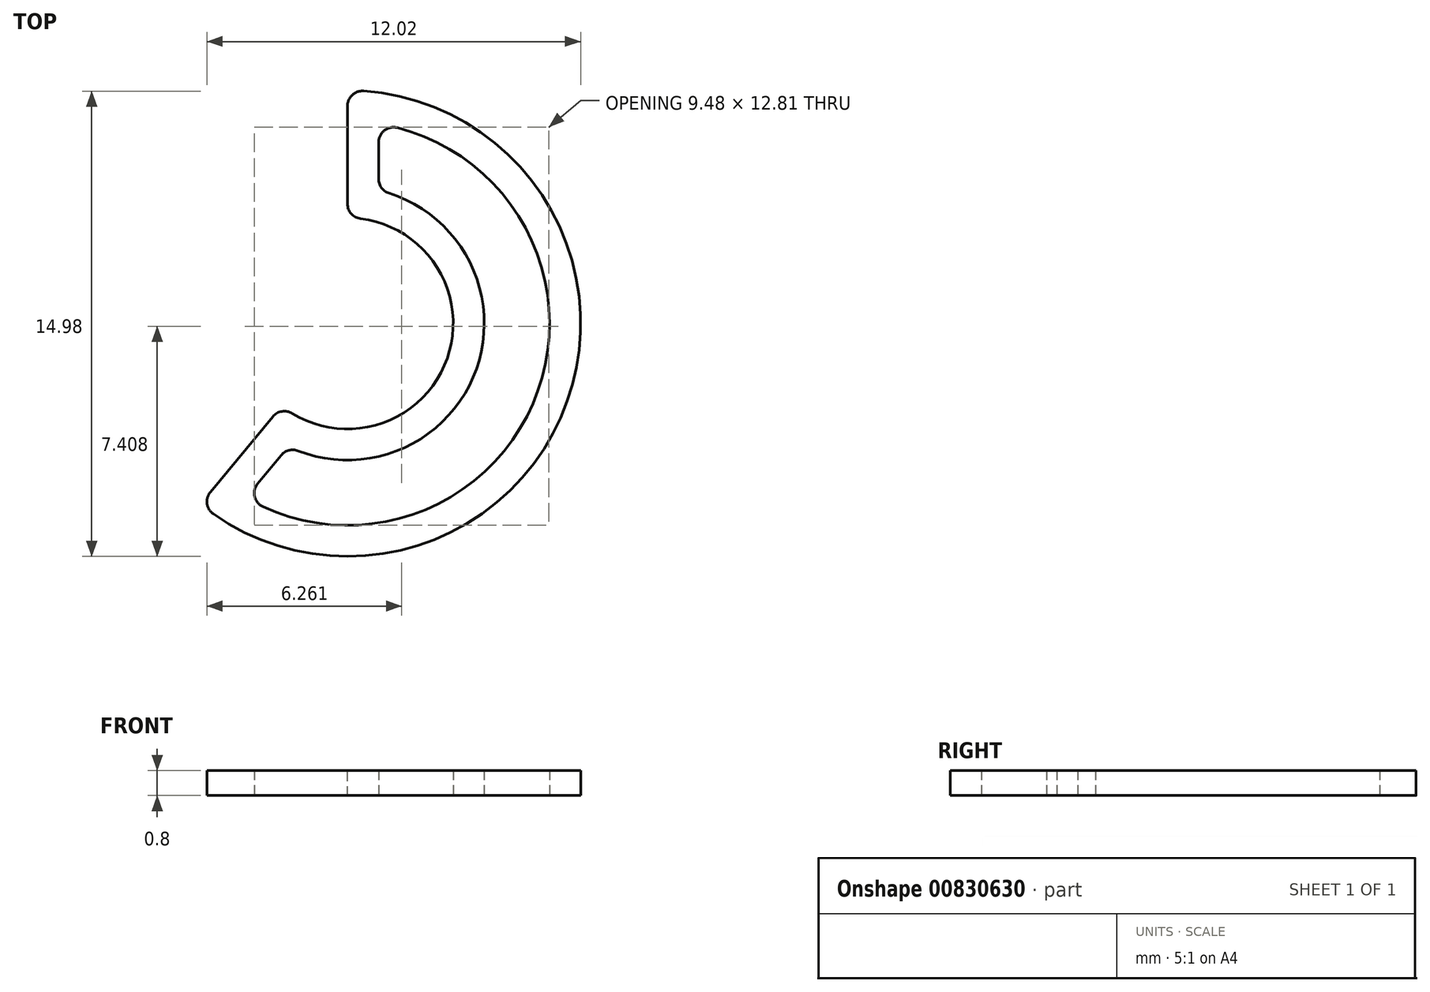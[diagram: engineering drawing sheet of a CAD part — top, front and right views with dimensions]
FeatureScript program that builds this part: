
annotation { "Feature Type Name" : "Feature", "Feature Type Description" : "" }
export const myFeature = defineFeature(function(context is Context, id is Id, definition is map)
    precondition{}
    {
        {
            var Q0;
            Q0=qCreatedBy(makeId("Top.planeOp"),FACE);
            var sketch = newSketch(context, id + "F0", { "sketchPlane" : qUnion([Q0])});
            skArc(sketch, "E0", {"start": v(-4.73, -5.82) * mm, "mid": v(7.07, -2.51) * mm, "end": v(0, 7.5) * mm});
            skArc(sketch, "E1", {"start": v(-2.12, -2.66) * mm, "mid": v(3.2, -1.12) * mm, "end": v(0, 3.4) * mm});
            skLineSegment(sketch, "E2", {"start": v(0, 3.4) * mm, "end": v(0, 7.5) * mm});
            skLineSegment(sketch, "E3", {"start": v(-2.12, -2.66) * mm, "end": v(-4.73, -5.82) * mm});
            skArc(sketch, "E4.0", {"start": v(-3.27, -5.62) * mm, "mid": v(6.13, -2.17) * mm, "end": v(1, 6.42) * mm});
            skLineSegment(sketch, "E4.1", {"start": v(-1.9, -3.97) * mm, "end": v(-3.27, -5.62) * mm});
            skArc(sketch, "E4.2", {"start": v(-1.9, -3.97) * mm, "mid": v(4.15, -1.46) * mm, "end": v(1, 4.28) * mm});
            skLineSegment(sketch, "E4.3", {"start": v(1, 4.28) * mm, "end": v(1, 6.42) * mm});
            skSolve(sketch);
        }
        {
            var Q0;
            {var subQ0=sQuery(id+"F0.wireOp",EDGE,"E2");Q0=makeQuery(id+"F0.imprint","IMPRINT",FACE,{"disambiguationData":[TD([[makeQuery(id+"F0.imprint","IMPRINT",EDGE,{"derivedFrom":subQ0}),-1.0]])]});}
            extrude(context, id + "F1", {"entities" : qUnion([Q0]), "depth" : .8 * mm, "offsetDistance" : 25 * mm});
        }
        {
            var Q0;
            Q0=makeQuery(id+"F1.opExtrude","SWEPT_EDGE",EDGE,{"disambiguationData":[OSD([sQuery(id+"F0.wireOp",EDGE,"E4.0"),sQuery(id+"F0.wireOp",EDGE,"E4.1")])]});
            var Q1;
            Q1=makeQuery(id+"F1.opExtrude","SWEPT_EDGE",EDGE,{"disambiguationData":[OSD([sQuery(id+"F0.wireOp",EDGE,"E4.1"),sQuery(id+"F0.wireOp",EDGE,"E4.2")])]});
            var Q2;
            Q2=makeQuery(id+"F1.opExtrude","SWEPT_EDGE",EDGE,{"disambiguationData":[OSD([sQuery(id+"F0.wireOp",EDGE,"E4.2"),sQuery(id+"F0.wireOp",EDGE,"E4.3")])]});
            var Q3;
            Q3=makeQuery(id+"F1.opExtrude","SWEPT_EDGE",EDGE,{"disambiguationData":[OSD([sQuery(id+"F0.wireOp",EDGE,"E4.0"),sQuery(id+"F0.wireOp",EDGE,"E4.3")])]});
            var Q4;
            Q4=makeQuery(id+"F1.opExtrude","SWEPT_EDGE",EDGE,{"disambiguationData":[OSD([sQuery(id+"F0.wireOp",EDGE,"E1"),sQuery(id+"F0.wireOp",EDGE,"E2")])]});
            var Q5;
            Q5=makeQuery(id+"F1.opExtrude","SWEPT_EDGE",EDGE,{"disambiguationData":[OSD([sQuery(id+"F0.wireOp",EDGE,"E1"),sQuery(id+"F0.wireOp",EDGE,"E3")])]});
            var Q6;
            Q6=makeQuery(id+"F1.opExtrude","SWEPT_EDGE",EDGE,{"disambiguationData":[OSD([sQuery(id+"F0.wireOp",EDGE,"E0"),sQuery(id+"F0.wireOp",EDGE,"E3")])]});
            var Q7;
            Q7=makeQuery(id+"F1.opExtrude","SWEPT_EDGE",EDGE,{"disambiguationData":[OSD([sQuery(id+"F0.wireOp",EDGE,"E0"),sQuery(id+"F0.wireOp",EDGE,"E2")])]});
            fillet(context, id + "F2", {"entities" : qUnion([Q0, Q1, Q2, Q3, Q4, Q5, Q6, Q7]), "radius" : 0.48 * mm, "tangentPropagation" : true, "allowEdgeOverflow" : false});
        }
    });
